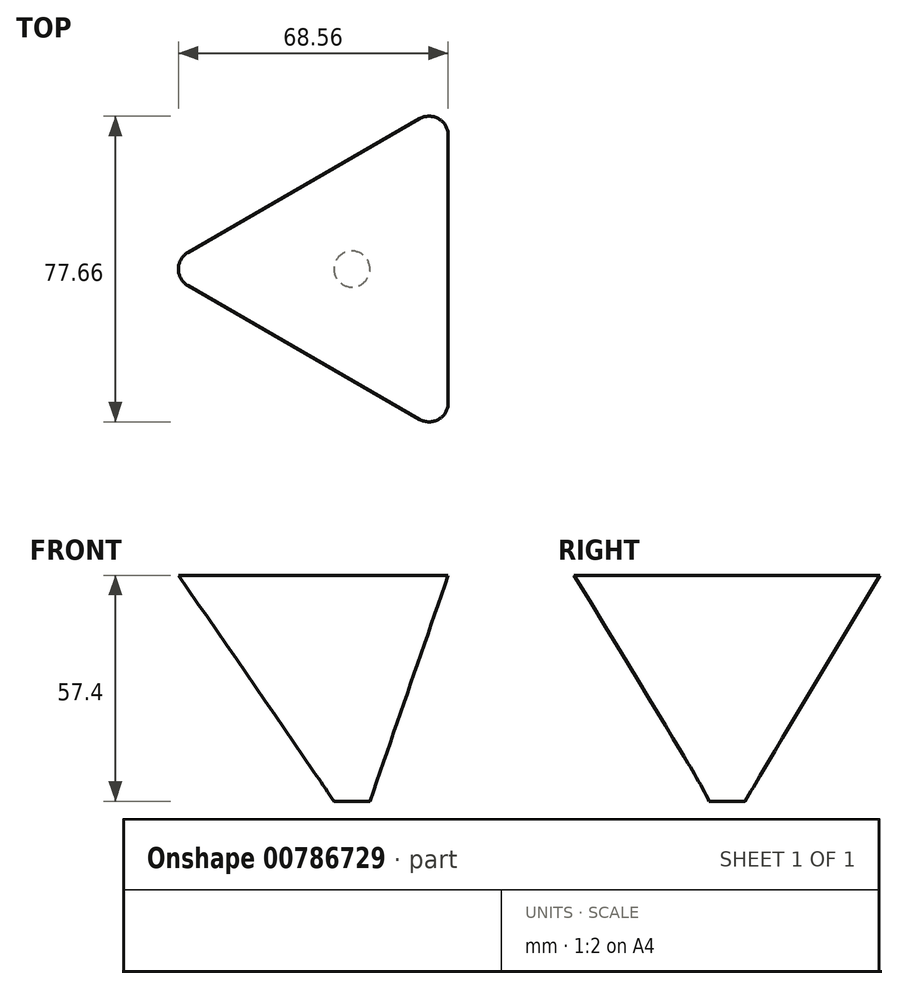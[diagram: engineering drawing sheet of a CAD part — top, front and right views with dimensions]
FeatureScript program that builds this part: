
annotation { "Feature Type Name" : "Feature", "Feature Type Description" : "" }
export const myFeature = defineFeature(function(context is Context, id is Id, definition is map)
    precondition{}
    {
        {
            var Q0;
            Q0=qCreatedBy(makeId("Top.planeOp"),FACE);
            var sketch = newSketch(context, id + "F0", { "sketchPlane" : qUnion([Q0])});
            skCircle(sketch, "E0.cCircle", {"center": v(0, 0) * mm, "radius": 24.47 * mm, "construction": true});
            skLineSegment(sketch, "E0.0", {"start": v(24.47, 34) * mm, "end": v(24.47, -34) * mm});
            skLineSegment(sketch, "E0.1", {"start": v(17.2, -38.18) * mm, "end": v(-41.67, -4.2) * mm});
            skLineSegment(sketch, "E0.2", {"start": v(-41.67, 4.2) * mm, "end": v(17.2, 38.18) * mm});
            skPoint(sketch, "E0.0.midPoint", {"position": v(24.47, 0) * mm});
            skPoint(sketch, "E1.visualSharp", {"position": v(24.47, -42.38) * mm});
            skArc(sketch, "E1.filletArc", {"start": v(17.2, -38.18) * mm, "mid": v(22.05, -38.18) * mm, "end": v(24.47, -34) * mm});
            skPoint(sketch, "E2.visualSharp", {"position": v(-48.93, 0) * mm});
            skArc(sketch, "E2.filletArc", {"start": v(-41.67, 4.2) * mm, "mid": v(-44.1, 0) * mm, "end": v(-41.67, -4.2) * mm});
            skPoint(sketch, "E3.visualSharp", {"position": v(24.47, 42.38) * mm});
            skArc(sketch, "E3.filletArc", {"start": v(24.47, 34) * mm, "mid": v(22.05, 38.18) * mm, "end": v(17.2, 38.18) * mm});
            skSolve(sketch);
        }
        {
            var Q0;
            Q0=qCreatedBy(makeId("Top.planeOp"),FACE);
            cPlane(context, id + "F1", {"entities" : qUnion([Q0]), "cplaneType" : CPlaneType.OFFSET, "offset" : 57.4 * mm, "oppositeDirection" : true, "width" : 152.4 * mm, "height" : 152.4 * mm});
        }
        {
            var Q0;
            Q0=qCreatedBy(id+"F1.planeOp",FACE);
            var sketch = newSketch(context, id + "F2", { "sketchPlane" : qUnion([Q0])});
            skCircle(sketch, "E4", {"center": v(0, 0) * mm, "radius": 4.57 * mm});
            skSolve(sketch);
        }
        {
            var Q0;
            Q0=makeQuery(id+"F0.imprint","IMPRINT",FACE,{"disambiguationData":[TD([[makeQuery(id+"F0.imprint","IMPRINT",EDGE,{"derivedFrom":sQuery(id+"F0.wireOp",EDGE,"E0.0")}),-1.0]])]});
            var Q1;
            Q1=makeQuery(id+"F2.imprint","IMPRINT",FACE,{"disambiguationData":[TD([[makeQuery(id+"F2.imprint","IMPRINT",EDGE,{"derivedFrom":sQuery(id+"F2.wireOp",EDGE,"E4")}),1.0]])]});
            loft(context, id + "F3", {"sheetProfilesArray" : [{ "sheetProfileEntities" : qUnion([Q0]) }, { "sheetProfileEntities" : qUnion([Q1]) }]});
        }
    });
